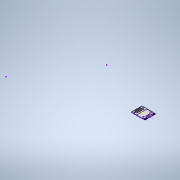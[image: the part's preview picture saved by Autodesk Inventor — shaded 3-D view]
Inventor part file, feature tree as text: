
AUTODESK INVENTOR PART (.ipt)
format: ipt  version: 2020 (Build 240168000, 168)  size: 15,622,656 bytes
history: native  units: mm
features: extrude x4, sketch x1, other x1
ambient origin geometry x8: Origin, YZ Plane, XZ Plane, XY Plane, X Axis, Y Axis, Z Axis, Center Point
bodies: Solid1 (feature_tree)
feature tree (6):
  sketch  "Sketch1"  dims[d45=20.0mm d46=0.0mm d48=14.0mm d49=0.0mm d50=10.0mm d51=0.0mm d52=3.0mm d53=0.0mm d47=0.5mm]
  extrude  "Extrusion1"  Depth=10.0mm TaperAngle=0.0deg
  extrude  "Extrusion2"  Depth=10.0mm TaperAngle=0.0deg
  extrude  "Extrusion3"  Depth=10.0mm TaperAngle=0.0deg
  extrude  "Extrusion4"  Depth=10.0mm
  other  "Image1"
